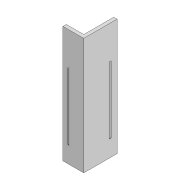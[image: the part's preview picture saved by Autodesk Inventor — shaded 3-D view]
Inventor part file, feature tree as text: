
AUTODESK INVENTOR PART (.ipt)
format: ipt  version: 2022 (Build 260153000, 153)  size: 132,608 bytes
history: native  units: mm
features: projected_geometry x6, extrude x3, sketch x3
ambient origin geometry x8: Origin, YZ Plane, XZ Plane, XY Plane, X Axis, Y Axis, Z Axis, Center Point
bodies: Solid1 (feature_tree)
feature tree (12):
  extrude  "Extrusion1"  Depth=4.0mm
  extrude  "Extrusion2"  Depth=25.0mm
  extrude  "Extrusion3"  TaperAngle=30.0deg  [1 undecoded]
  sketch  "Sketch1"  dims[d0=4.0mm d1=4.0mm]
  sketch  "Sketch2"  dims[d2=40.0mm d3=25.0mm]
  projected_geometry  "Projected Loop1"
  sketch  "Sketch3"  dims[d4=100.0mm d5=0.0mm d7=30.0deg d8=1.0mm d9=80.0mm d10=0.0mm d11=20.0mm d12=40.0mm d13=0.0mm]
  projected_geometry  "Projected Loop2"
  projected_geometry  "Projected Loop3"
  projected_geometry  "Projected Loop4"
  projected_geometry  "Projected Loop5"
  projected_geometry  "Projected Loop6"
note: 1 required parameter value undecoded (feature->parameter linkage not recoverable at this tier; creation-order binding heuristic only, values carry confidence <= 0.55)
